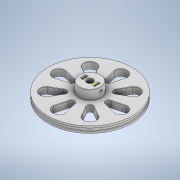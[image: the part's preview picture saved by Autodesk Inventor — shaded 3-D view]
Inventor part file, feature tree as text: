
AUTODESK INVENTOR PART (.ipt)
format: ipt  version: 2020 (Build 240168000, 168)  size: 427,520 bytes
history: native  units: in
note: dims shown in document units (in); Inventor stores cm internally (conversion verified against a paired STEP export)
features: sketch x16, extrude x12, fillet x4
ambient origin geometry x8: Origin, YZ Plane, XZ Plane, XY Plane, X Axis, Y Axis, Z Axis, Center Point
bodies: Solid1 (feature_tree)
feature tree (32):
  extrude  "Extrusion1"  Depth=0.0787in TaperAngle=0.0deg
  sketch  "Sketch2"  dims[d3=3.4646in d4=0.1181in d5=0.0in]
  sketch  "Sketch3"  dims[d6=0.0787in d7=0.0in d8=0.9055in]
  extrude  "Extrusion2"  Depth=0.1181in TaperAngle=0.0deg
  extrude  "Extrusion3"  Depth=0.9055in
  extrude  "Extrusion4"  Depth=0.3937in
  extrude  "Extrusion5"  Depth=0.1083in
  extrude  "Extrusion6"  Depth=0.0945in
  sketch  "Sketch8"  dims[d23=0.7362in d24=0.0in d26=0.1378in d27=0.2362in d28=0.0in d30=0.1378in]
  extrude  "Extrusion7"  Depth=0.2362in TaperAngle=0.0deg
  extrude  "Extrusion8"  Depth=0.1378in
  fillet  "Fillet1"  Radius=0.2362in
  fillet  "Fillet2"  Radius=0.1378in
  extrude  "Extrusion9"  Depth=0.0162in
  fillet  "Fillet3"  Radius=0.0162in
  fillet  "Fillet4"  Radius=0.5118in
  extrude  "Extrusion10"  Depth=0.2362in
  extrude  "Extrusion11"  Depth=0.2362in
  sketch  "Sketch14"  dims[d57=0.7874in]
  sketch  "Sketch15"  dims[d60=0.2362in]
  extrude  "Extrusion12"  Depth=0.5118in
  sketch  "Sketch1"  dims[d0=3.5433in d1=0.0787in d2=0.0in]
  sketch  "Sketch4"  dims[d9=0.3937in d10=0.0in d12=0.2362in]
  sketch  "Sketch5"  dims[d15=0.1083in d16=0.1083in]
  sketch  "Sketch6"  dims[d17=0.0945in d19=0.0945in]
  sketch  "Sketch7"  dims[d20=0.2165in d21=0.2362in d22=0.0in]
  sketch  "Sketch9"  dims[d31=0.3263in d32=0.0in d33=0.0162in d34=0.0162in d36=0.5118in]
  sketch  "Sketch10"  dims[d38=0.2362in d40=0.2362in]
  sketch  "Sketch11"  dims[d42=0.5118in d45=0.2362in]
  sketch  "Sketch12"  dims[d46=0.2362in d49=0.5118in]
  sketch  "Sketch13"  dims[d50=0.5118in]
  sketch  "Sketch16"  dims[d61=0.5118in d62=0.2362in d63=0.5118in d64=0.5118in d65=0.2362in d66=0.2362in d67=0.5118in d68=1.9513in d69=0.0in d70=0.0162in d71=0.0162in d72=2.3563in d73=0.0in d74=0.1181in d75=0.2362in d76=0.1181in d77=0.2362in d78=0.2362in d79=0.0in d81=0.1378in d82=0.4237in d83=0.0in d29=0.1969in]
